# Revit family: Access_Door_ACUDOR_Universal-Flush_ED-2002
name_source: partatom
category: Doors
revit_build: Autodesk Revit 2017 (Build: 20171027_0315(x64)
units: mm (PartAtom-declared; Revit-internal decimal feet)

## family parameters
Cut with Voids When Loaded = No
Host = Face
Room Calculation Point = No
Shared = No

## types (10) — shared parameters
Analytic Construction = <None>
Default Elevation = 48 "
Description = FLUSH ACCESS DOOR
Manufacturer = ACUDOR
Material Finish = Metal - Acudor - Stainless - Polished
URL = www.acudor.com
zero-valued in all types: Thickness, Wall Offset

## per-type parameters (varying)
| type | Height | Width |
| ED-2002-0606 | 8 " | 8.125 " |
| ED-2002-0808 | 10 " | 10.125 " |
| ED-2002-1010 | 12 " | 12.125 " |
| ED-2002-1212 | 14 " | 14.125 " |
| ED-2002-1414 | 16 " | 16.125 " |
| ED-2002-1616 | 18 " | 18.125 " |
| ED-2002-1818 | 20 " | 20.125 " |
| ED-2002-2020 | 22 " | 22.125 " |
| ED-2002-2424 | 26 " | 26.125 " |
| ED-2002-2436 | 38 " | 26.125 " |

note: column(s) folded — value = type name in every type: Model

## geometry (parser evidence)
native form markers: Blend x2, Sweep x3
no freeform markers — native parametric forms only
